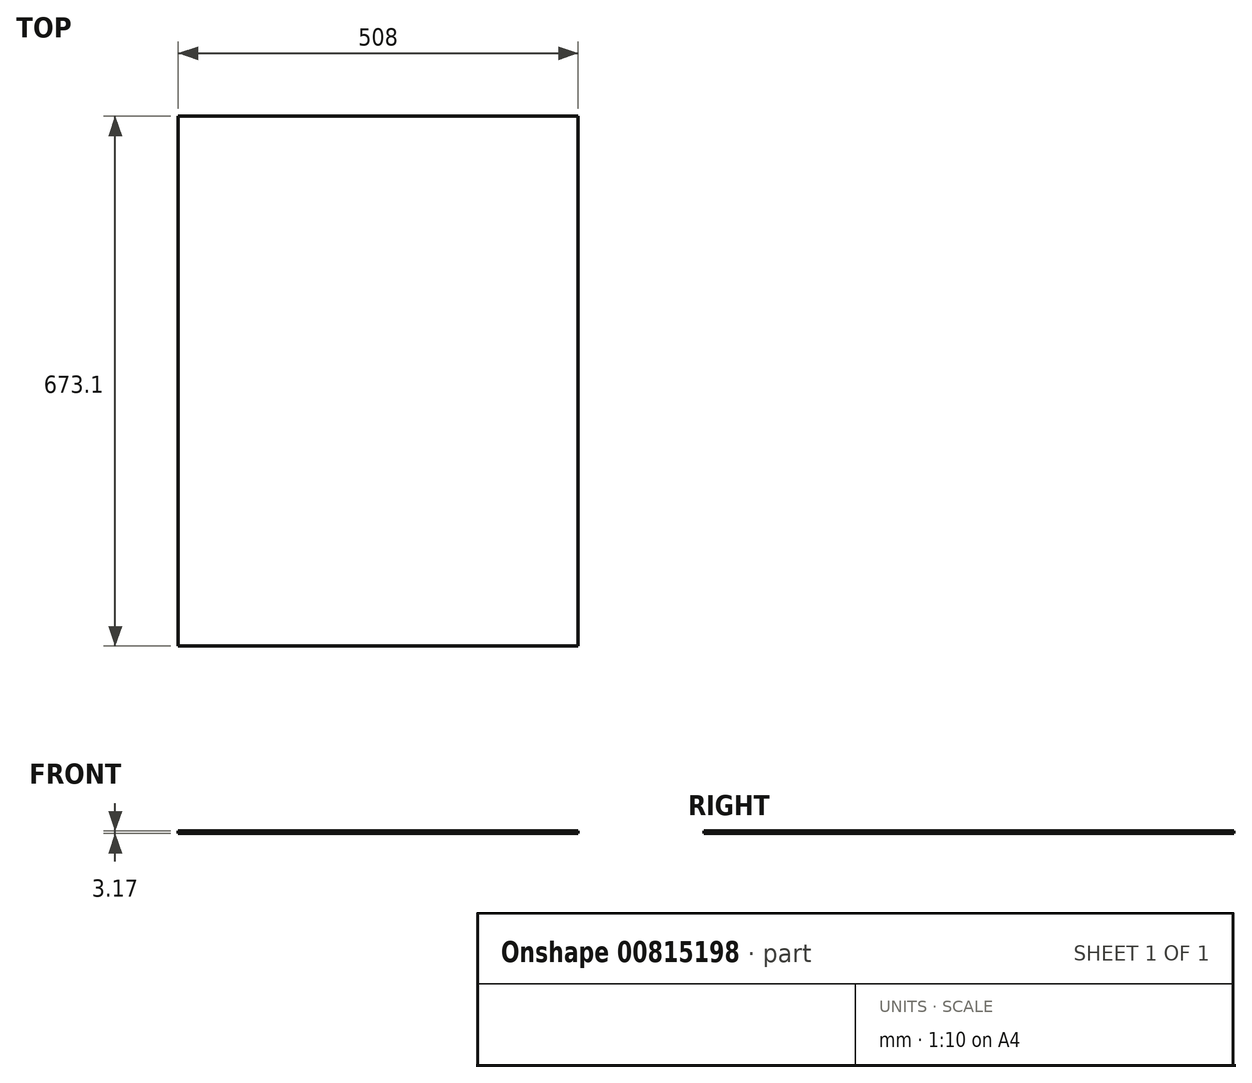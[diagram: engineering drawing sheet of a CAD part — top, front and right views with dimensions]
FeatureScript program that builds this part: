
annotation { "Feature Type Name" : "Feature", "Feature Type Description" : "" }
export const myFeature = defineFeature(function(context is Context, id is Id, definition is map)
    precondition{}
    {
        {
            var Q0;
            Q0=qCreatedBy(makeId("Top.planeOp"),FACE);
            var sketch = newSketch(context, id + "F0", { "sketchPlane" : qUnion([Q0])});
            skLineSegment(sketch, "E0.bottom", {"start": v(0, 0) * mm, "end": v(508, 0) * mm});
            skLineSegment(sketch, "E0.top", {"start": v(0, -673.1) * mm, "end": v(508, -673.1) * mm});
            skLineSegment(sketch, "E0.left", {"start": v(0, 0) * mm, "end": v(0, -673.1) * mm});
            skLineSegment(sketch, "E0.right", {"start": v(508, 0) * mm, "end": v(508, -673.1) * mm});
            skText(sketch, "E1", { "text": "1\n0\n7\n2", "fontName": "OpenSans-Regular.ttf"});
            const initialGuessF0  = {"E1": [0.2286, -0.11312, 1, 0, 0.06232]};
            skSetInitialGuess(sketch, initialGuessF0);
            skSolve(sketch);
        }
        {
            var Q0;
            Q0 = qSketchRegion(id + "F0", true);
            var Q1;
            Q1=makeQuery(id+"F0.imprint","IMPRINT",FACE,{"disambiguationData":[TD([[makeQuery(id+"F0.imprint","IMPRINT",EDGE,{"derivedFrom":sQuery(id+"F0.wireOp",EDGE,"E1.sketch_text.stroke-9")}),-1.0]])]});
            var Q2;
            Q2=makeQuery(id+"F0.imprint","IMPRINT",FACE,{"disambiguationData":[TD([[makeQuery(id+"F0.imprint","IMPRINT",EDGE,{"derivedFrom":sQuery(id+"F0.wireOp",EDGE,"E1.sketch_text.stroke-17")}),1.0]])]});
            var Q3;
            Q3=makeQuery(id+"F0.imprint","IMPRINT",FACE,{"disambiguationData":[TD([[makeQuery(id+"F0.imprint","IMPRINT",EDGE,{"derivedFrom":sQuery(id+"F0.wireOp",EDGE,"E1.sketch_text.stroke-0")}),-1.0]])]});
            var Q4;
            Q4=makeQuery(id+"F0.imprint","IMPRINT",FACE,{"disambiguationData":[TD([[makeQuery(id+"F0.imprint","IMPRINT",EDGE,{"derivedFrom":sQuery(id+"F0.wireOp",EDGE,"E1.sketch_text.stroke-32")}),-1.0]])]});
            var Q5;
            Q5=makeQuery(id+"F0.imprint","IMPRINT",FACE,{"disambiguationData":[TD([[makeQuery(id+"F0.imprint","IMPRINT",EDGE,{"derivedFrom":sQuery(id+"F0.wireOp",EDGE,"E1.sketch_text.stroke-25")}),-1.0]])]});
            extrude(context, id + "F1", {"entities" : qUnion([Q0, Q1, Q2, Q3, Q4, Q5]), "depth" : 3.17 * mm, "offsetDistance" : 25.4 * mm});
        }
    });
